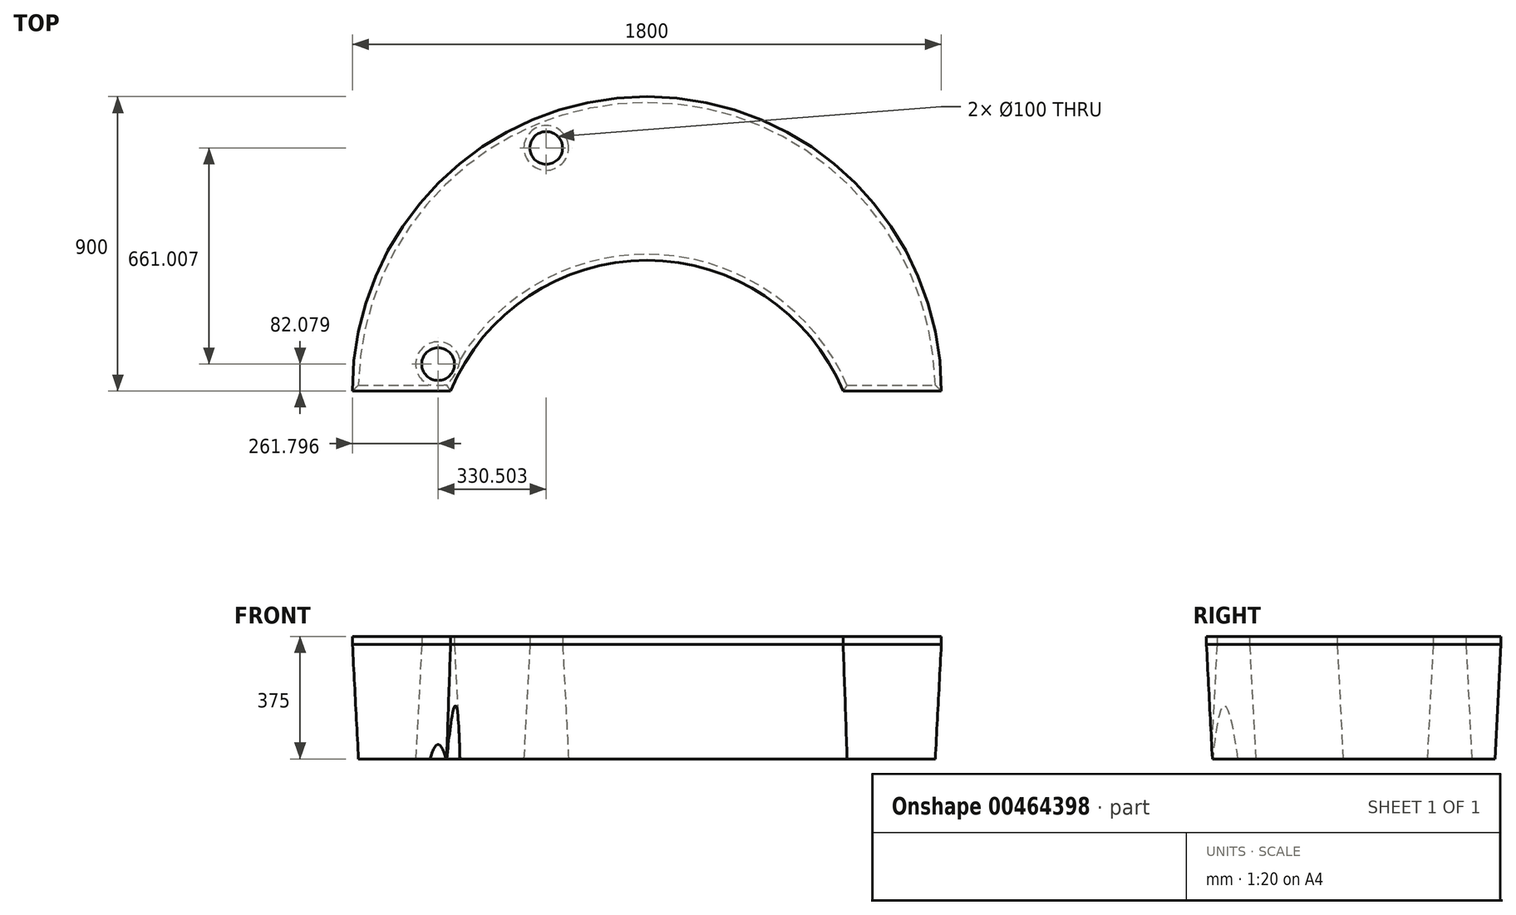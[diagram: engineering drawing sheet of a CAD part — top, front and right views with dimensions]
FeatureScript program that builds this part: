
annotation { "Feature Type Name" : "Feature", "Feature Type Description" : "" }
export const myFeature = defineFeature(function(context is Context, id is Id, definition is map)
    precondition{}
    {
        {
            var Q0;
            Q0=qCreatedBy(makeId("Top.planeOp"),FACE);
            var sketch = newSketch(context, id + "F0", { "sketchPlane" : qUnion([Q0])});
            skLineSegment(sketch, "E0", {"start": v(-988.02, 0) * mm, "end": v(1076.13, 0) * mm, "construction": true});
            skCircle(sketch, "E1", {"center": v(0, 0) * mm, "radius": 900 * mm});
            skCircle(sketch, "E2", {"center": v(0, 0) * mm, "radius": 600 * mm, "construction": true});
            skCircle(sketch, "E3", {"center": v(0, 0) * mm, "radius": 400 * mm, "construction": true});
            skLineSegment(sketch, "E4", {"start": v(-900, 0) * mm, "end": v(-600, 0) * mm});
            skArc(sketch, "E5", {"start": v(600, 0) * mm, "mid": v(0, 399.5) * mm, "end": v(-600, 0) * mm});
            skLineSegment(sketch, "E6", {"start": v(600, 0) * mm, "end": v(900, 0) * mm});
            skLineSegment(sketch, "E7", {"start": v(0, 900) * mm, "end": v(0, 400) * mm, "construction": true});
            skArc(sketch, "E8", {"start": v(750, 0) * mm, "mid": v(0, 650) * mm, "end": v(-750, 0) * mm, "construction": true});
            skCircle(sketch, "E9", {"center": v(638.2, 82.08) * mm, "radius": 50 * mm});
            skCircle(sketch, "E10", {"center": v(307.7, 743.09) * mm, "radius": 50 * mm});
            skCircle(sketch, "E11.MirrorC", {"center": v(-638.2, 82.08) * mm, "radius": 50 * mm});
            skCircle(sketch, "E12.MirrorC", {"center": v(-307.7, 743.09) * mm, "radius": 50 * mm});
            skSolve(sketch);
        }
        {
            var Q0;
            {var subQ0=sQuery(id+"F0.wireOp",EDGE,"E4");Q0=makeQuery(id+"F0.imprint","IMPRINT",FACE,{"disambiguationData":[TD([[makeQuery(id+"F0.imprint","IMPRINT",EDGE,{"derivedFrom":subQ0}),1.0]])]});}
            var Q1;
            Q1=makeQuery(id+"F0.imprint","IMPRINT",FACE,{"disambiguationData":[TD([[makeQuery(id+"F0.imprint","IMPRINT",EDGE,{"derivedFrom":sQuery(id+"F0.wireOp",EDGE,"E11.MirrorC")}),-1.0]])]});
            var Q2;
            Q2=makeQuery(id+"F0.imprint","IMPRINT",FACE,{"disambiguationData":[TD([[makeQuery(id+"F0.imprint","IMPRINT",EDGE,{"derivedFrom":sQuery(id+"F0.wireOp",EDGE,"E12.MirrorC")}),-1.0]])]});
            var Q3;
            Q3=makeQuery(id+"F0.imprint","IMPRINT",FACE,{"disambiguationData":[TD([[makeQuery(id+"F0.imprint","IMPRINT",EDGE,{"derivedFrom":sQuery(id+"F0.wireOp",EDGE,"E10")}),1.0]])]});
            var Q4;
            Q4=makeQuery(id+"F0.imprint","IMPRINT",FACE,{"disambiguationData":[TD([[makeQuery(id+"F0.imprint","IMPRINT",EDGE,{"derivedFrom":sQuery(id+"F0.wireOp",EDGE,"E9")}),1.0]])]});
            extrude(context, id + "F1", {"entities" : qUnion([Q0, Q1, Q2, Q3, Q4]), "depth" : 25 * mm});
        }
        {
            var Q0;
            Q0=makeQuery(id+"F0.imprint","IMPRINT",FACE,{"disambiguationData":[TD([[makeQuery(id+"F0.imprint","IMPRINT",EDGE,{"derivedFrom":sQuery(id+"F0.wireOp",EDGE,"E11.MirrorC")}),-1.0]])]});
            var Q1;
            Q1=makeQuery(id+"F0.imprint","IMPRINT",FACE,{"disambiguationData":[TD([[makeQuery(id+"F0.imprint","IMPRINT",EDGE,{"derivedFrom":sQuery(id+"F0.wireOp",EDGE,"E12.MirrorC")}),-1.0]])]});
            var Q2;
            Q2=makeQuery(id+"F0.imprint","IMPRINT",FACE,{"disambiguationData":[TD([[makeQuery(id+"F0.imprint","IMPRINT",EDGE,{"derivedFrom":sQuery(id+"F0.wireOp",EDGE,"E10")}),1.0]])]});
            var Q3;
            Q3=makeQuery(id+"F0.imprint","IMPRINT",FACE,{"disambiguationData":[TD([[makeQuery(id+"F0.imprint","IMPRINT",EDGE,{"derivedFrom":sQuery(id+"F0.wireOp",EDGE,"E9")}),1.0]])]});
            extrude(context, id + "F2", {"entities" : qUnion([Q0, Q1, Q2, Q3]), "oppositeDirection" : true, "depth" : 350 * mm, "hasDraft" : true, "draftAngle" : 3 * degree, "draftPullDirection" : true});
        }
    });
